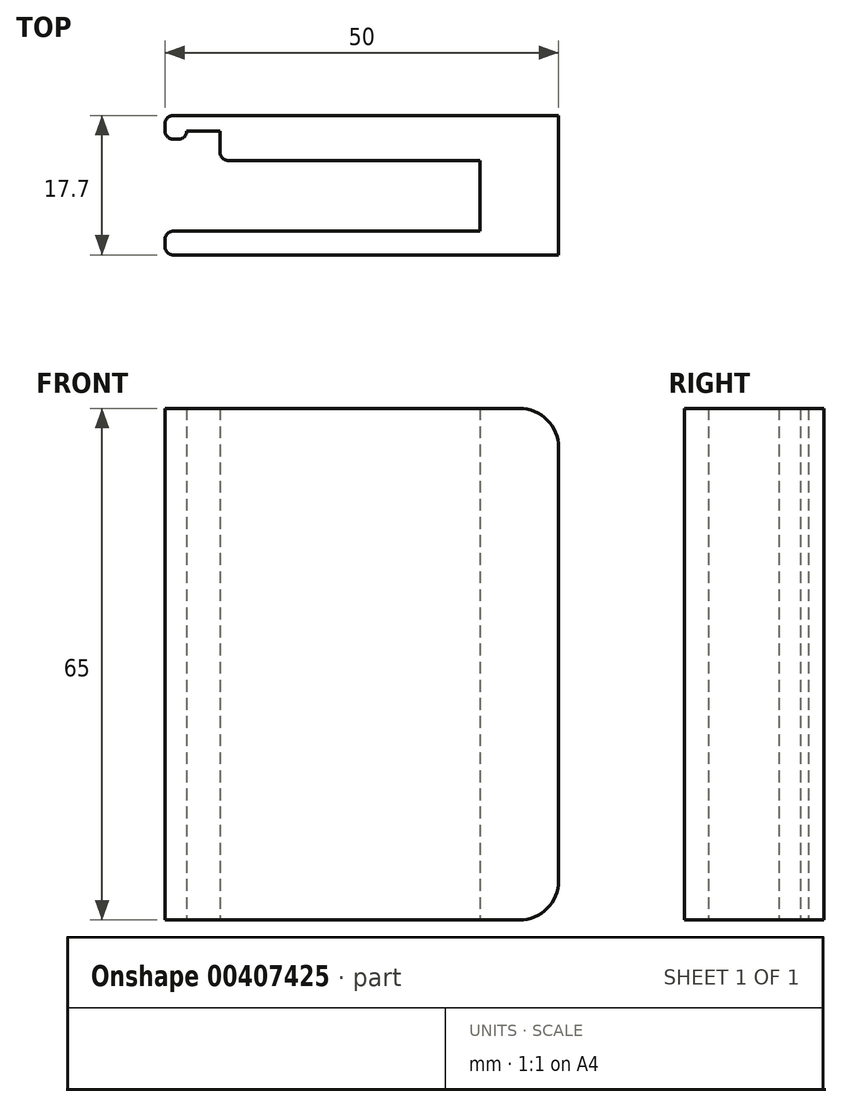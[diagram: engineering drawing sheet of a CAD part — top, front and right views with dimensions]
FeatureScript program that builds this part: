
annotation { "Feature Type Name" : "Feature", "Feature Type Description" : "" }
export const myFeature = defineFeature(function(context is Context, id is Id, definition is map)
    precondition{}
    {
        {
            var Q0;
            Q0=qCreatedBy(makeId("Top.planeOp"),FACE);
            var sketch = newSketch(context, id + "F0", { "sketchPlane" : qUnion([Q0])});
            skLineSegment(sketch, "E0.bottom", {"start": v(0, 12.36) * mm, "end": v(-49, 12.36) * mm});
            skLineSegment(sketch, "E0.top", {"start": v(0, -5.34) * mm, "end": v(-49, -5.34) * mm});
            skLineSegment(sketch, "E0.left", {"start": v(0, 12.36) * mm, "end": v(0, -5.34) * mm});
            skLineSegment(sketch, "E0.right", {"start": v(-50, 11.36) * mm, "end": v(-50, 10.36) * mm});
            skLineSegment(sketch, "E1", {"start": v(-10, -2.34) * mm, "end": v(-49, -2.34) * mm});
            skLineSegment(sketch, "E2", {"start": v(-10, -2.34) * mm, "end": v(-10, 6.66) * mm});
            skLineSegment(sketch, "E3", {"start": v(-10, 6.66) * mm, "end": v(-42, 6.66) * mm});
            skLineSegment(sketch, "E4", {"start": v(-43, 7.66) * mm, "end": v(-43, 10.36) * mm});
            skLineSegment(sketch, "E5", {"start": v(-43, 10.36) * mm, "end": v(-47.25, 10.36) * mm});
            skLineSegment(sketch, "E6", {"start": v(-47.25, 10.36) * mm, "end": v(-47.25, 10.36) * mm});
            skLineSegment(sketch, "E7", {"start": v(-48.25, 9.36) * mm, "end": v(-49, 9.36) * mm});
            skLineSegment(sketch, "E8.trimOffspring", {"start": v(-50, -3.34) * mm, "end": v(-50, -4.34) * mm});
            skPoint(sketch, "E9.visualSharp", {"position": v(-50, -5.34) * mm});
            skArc(sketch, "E9.filletArc", {"start": v(-50, -4.34) * mm, "mid": v(-49.7, -5.05) * mm, "end": v(-49, -5.34) * mm});
            skPoint(sketch, "E10.visualSharp", {"position": v(-50, -2.34) * mm});
            skArc(sketch, "E10.filletArc", {"start": v(-49, -2.34) * mm, "mid": v(-49.7, -2.64) * mm, "end": v(-50, -3.34) * mm});
            skPoint(sketch, "E11.visualSharp", {"position": v(-43, 6.66) * mm});
            skArc(sketch, "E11.filletArc", {"start": v(-43, 7.66) * mm, "mid": v(-42.7, 6.95) * mm, "end": v(-42, 6.66) * mm});
            skPoint(sketch, "E12.visualSharp", {"position": v(-50, 9.36) * mm});
            skArc(sketch, "E12.filletArc", {"start": v(-50, 10.36) * mm, "mid": v(-49.7, 9.65) * mm, "end": v(-49, 9.36) * mm});
            skPoint(sketch, "E13.visualSharp", {"position": v(-47.25, 9.36) * mm});
            skArc(sketch, "E13.filletArc", {"start": v(-48.25, 9.36) * mm, "mid": v(-47.54, 9.65) * mm, "end": v(-47.25, 10.36) * mm});
            skPoint(sketch, "E14.visualSharp", {"position": v(-50, 12.36) * mm});
            skArc(sketch, "E14.filletArc", {"start": v(-49, 12.36) * mm, "mid": v(-49.7, 12.06) * mm, "end": v(-50, 11.36) * mm});
            skPoint(sketch, "E15.visualSharp", {"position": v(0, 12.36) * mm});
            skPoint(sketch, "E16.visualSharp", {"position": v(0, -5.34) * mm});
            skSolve(sketch);
        }
        {
            var Q0;
            Q0 = qSketchRegion(id + "F0", true);
            extrude(context, id + "F1", {"entities" : qUnion([Q0]), "endBound" : BoundingType.SYMMETRIC, "depth" : 65 * mm, "offsetDistance" : 25 * mm});
        }
        {
            var Q0;
            Q0=makeQuery(id+"F1.opExtrude","CAP_EDGE",EDGE,{"disambiguationData":[OSD([sQuery(id+"F0.wireOp",EDGE,"E0.left")])],"isStart":false});
            var Q1;
            Q1=makeQuery(id+"F1.opExtrude","CAP_EDGE",EDGE,{"disambiguationData":[OSD([sQuery(id+"F0.wireOp",EDGE,"E0.left")])],"isStart":true});
            fillet(context, id + "F2", {"entities" : qUnion([Q0, Q1]), "radius" : 5 * mm, "tangentPropagation" : true, "allowEdgeOverflow" : false});
        }
    });
